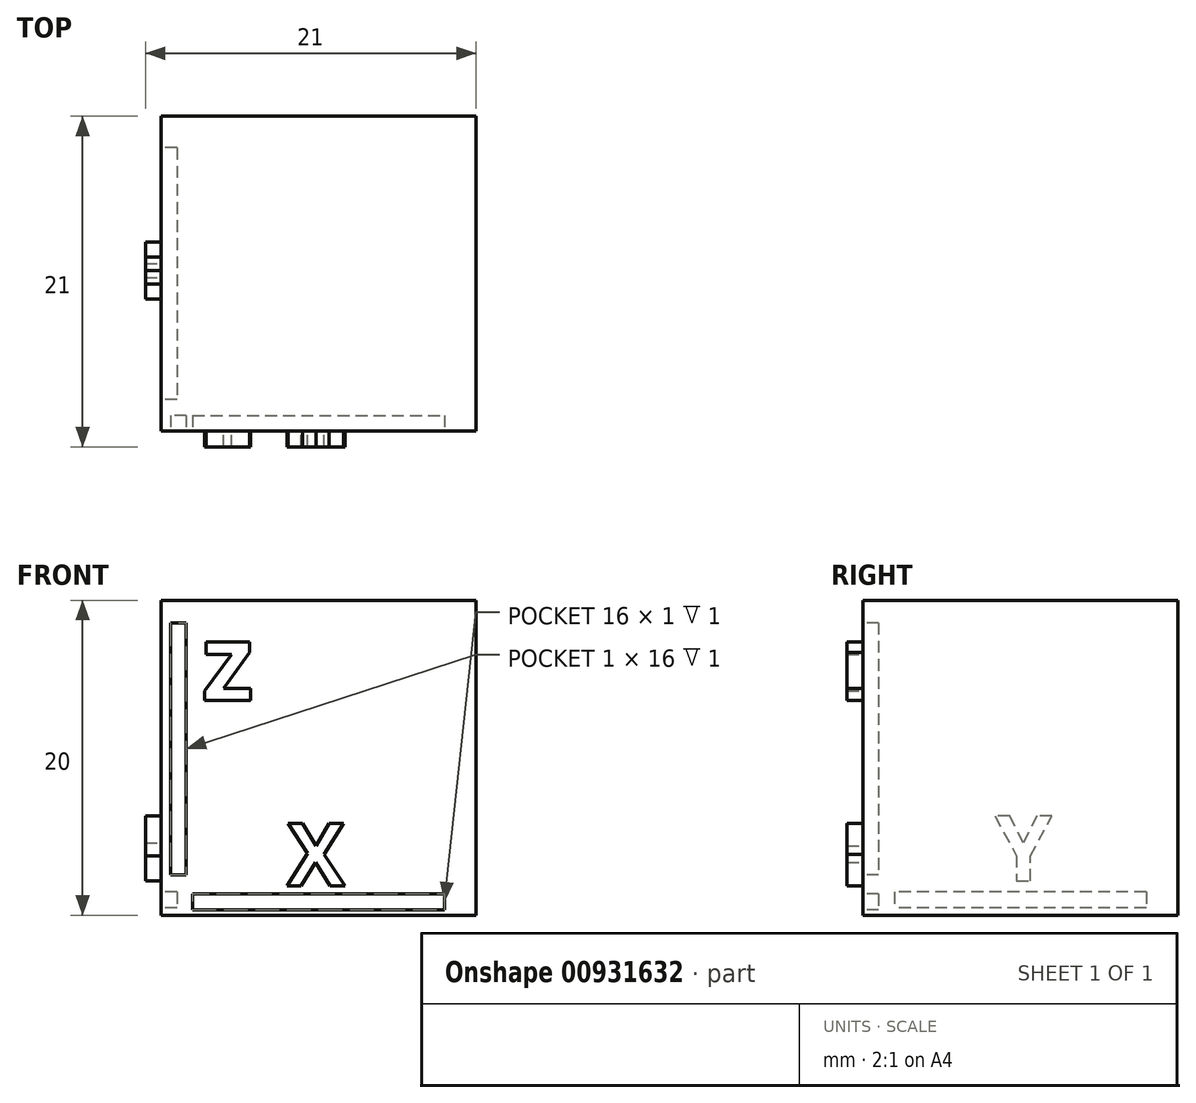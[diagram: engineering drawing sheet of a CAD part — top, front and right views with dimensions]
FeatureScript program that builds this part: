
annotation { "Feature Type Name" : "Feature", "Feature Type Description" : "" }
export const myFeature = defineFeature(function(context is Context, id is Id, definition is map)
    precondition{}
    {
        {
            var Q0;
            Q0=qCreatedBy(makeId("Top.planeOp"),FACE);
            var sketch = newSketch(context, id + "F0", { "sketchPlane" : qUnion([Q0])});
            skLineSegment(sketch, "E0.bottom", {"start": v(10, 10) * mm, "end": v(-10, 10) * mm});
            skLineSegment(sketch, "E0.top", {"start": v(10, -10) * mm, "end": v(-10, -10) * mm});
            skLineSegment(sketch, "E0.left", {"start": v(10, 10) * mm, "end": v(10, -10) * mm});
            skLineSegment(sketch, "E0.right", {"start": v(-10, 10) * mm, "end": v(-10, -10) * mm});
            skPoint(sketch, "E0.middle", {"position": v(0, 0) * mm});
            skSolve(sketch);
        }
        {
            var Q0;
            Q0=makeQuery(id+"F0.imprint","IMPRINT",FACE,{"disambiguationData":[TD([[makeQuery(id+"F0.imprint","IMPRINT",EDGE,{"derivedFrom":sQuery(id+"F0.wireOp",EDGE,"E0.bottom")}),1.0]])]});
            extrude(context, id + "F1", {"entities" : qUnion([Q0]), "depth" : 20 * mm, "offsetDistance" : 25 * mm});
        }
        {
            var Q0;
            Q0=makeQuery(id+"F1.opExtrude","SWEPT_FACE",FACE,{"disambiguationData":[OSD([sQuery(id+"F0.wireOp",EDGE,"E0.top")])]});
            var sketch = newSketch(context, id + "F2", { "sketchPlane" : qUnion([Q0])});
            skText(sketch, "E1", { "text": "z", "fontName": "OpenSans-Bold.ttf"});
            skText(sketch, "E2", { "text": "X", "fontName": "OpenSans-Bold.ttf"});
            skLineSegment(sketch, "E3.bottom", {"start": v(-8.4, 18.58) * mm, "end": v(-9.4, 18.58) * mm});
            skLineSegment(sketch, "E3.top", {"start": v(-8.4, 2.58) * mm, "end": v(-9.4, 2.58) * mm});
            skLineSegment(sketch, "E3.left", {"start": v(-8.4, 18.58) * mm, "end": v(-8.4, 2.58) * mm});
            skLineSegment(sketch, "E3.right", {"start": v(-9.4, 18.58) * mm, "end": v(-9.4, 2.58) * mm});
            skLineSegment(sketch, "E4.bottom", {"start": v(-8, 1.35) * mm, "end": v(8, 1.35) * mm});
            skLineSegment(sketch, "E4.top", {"start": v(-8, 0.35) * mm, "end": v(8, 0.35) * mm});
            skLineSegment(sketch, "E4.left", {"start": v(-8, 1.35) * mm, "end": v(-8, 0.35) * mm});
            skLineSegment(sketch, "E4.right", {"start": v(8, 1.35) * mm, "end": v(8, 0.35) * mm});
            skLineSegment(sketch, "E5", {"start": v(0, 0) * mm, "end": v(0, 20) * mm, "construction": true});
            const initialGuessF2  = {"E1": [-0.00743, 0.01364, 1, 0, 0.0049], "E2": [-0.00202, 0.00188, 1, 0, 0.00398]};
            skSetInitialGuess(sketch, initialGuessF2);
            skSolve(sketch);
        }
        {
            var Q0;
            Q0=makeQuery(id+"F1.opExtrude","SWEPT_FACE",FACE,{"disambiguationData":[OSD([sQuery(id+"F0.wireOp",EDGE,"E0.right")])]});
            var sketch = newSketch(context, id + "F3", { "sketchPlane" : qUnion([Q0])});
            skText(sketch, "E6", { "text": "Y", "fontName": "OpenSans-Bold.ttf"});
            skLineSegment(sketch, "E7.bottom", {"start": v(-8, 1.48) * mm, "end": v(8, 1.48) * mm});
            skLineSegment(sketch, "E7.top", {"start": v(-8, 0.48) * mm, "end": v(8, 0.48) * mm});
            skLineSegment(sketch, "E7.left", {"start": v(-8, 1.48) * mm, "end": v(-8, 0.48) * mm});
            skLineSegment(sketch, "E7.right", {"start": v(8, 1.48) * mm, "end": v(8, 0.48) * mm});
            skLineSegment(sketch, "E8", {"start": v(0, 0) * mm, "end": v(0, 20) * mm, "construction": true});
            skLineSegment(sketch, "E9", {"start": v(0, 1.48) * mm, "end": v(0, 0.48) * mm, "construction": true});
            const initialGuessF3  = {"E6": [-0.002, 0.00218, 1, 0, 0.00416]};
            skSetInitialGuess(sketch, initialGuessF3);
            skSolve(sketch);
        }
        {
            var Q0;
            Q0=makeQuery(id+"F2.imprint","IMPRINT",FACE,{"disambiguationData":[TD([[makeQuery(id+"F2.imprint","IMPRINT",EDGE,{"derivedFrom":sQuery(id+"F2.wireOp",EDGE,"E3.bottom")}),1.0]])]});
            var Q1;
            Q1=makeQuery(id+"F2.imprint","IMPRINT",FACE,{"disambiguationData":[TD([[makeQuery(id+"F2.imprint","IMPRINT",EDGE,{"derivedFrom":sQuery(id+"F2.wireOp",EDGE,"E4.bottom")}),-1.0]])]});
            extrude(context, id + "F4", {"entities" : qUnion([Q0, Q1]), "operationType" : NewBodyOperationType.REMOVE, "oppositeDirection" : true, "depth" : 1 * mm, "offsetDistance" : 25 * mm});
        }
        {
            var Q0;
            Q0=makeQuery(id+"F3.imprint","IMPRINT",FACE,{"disambiguationData":[TD([[makeQuery(id+"F3.imprint","IMPRINT",EDGE,{"derivedFrom":sQuery(id+"F3.wireOp",EDGE,"E7.bottom")}),-1.0]])]});
            extrude(context, id + "F5", {"entities" : qUnion([Q0]), "operationType" : NewBodyOperationType.REMOVE, "oppositeDirection" : true, "depth" : 1 * mm, "offsetDistance" : 25 * mm});
        }
        {
            var Q0;
            Q0=makeQuery(id+"F3.imprint","IMPRINT",FACE,{"disambiguationData":[TD([[makeQuery(id+"F3.imprint","IMPRINT",EDGE,{"derivedFrom":sQuery(id+"F3.wireOp",EDGE,"E6.sketch_text.stroke-0")}),-1.0]])]});
            extrude(context, id + "F6", {"entities" : qUnion([Q0]), "operationType" : NewBodyOperationType.ADD, "depth" : 1 * mm, "offsetDistance" : 25 * mm});
        }
        {
            var Q0;
            Q0=makeQuery(id+"F2.imprint","IMPRINT",FACE,{"disambiguationData":[TD([[makeQuery(id+"F2.imprint","IMPRINT",EDGE,{"derivedFrom":sQuery(id+"F2.wireOp",EDGE,"E1.sketch_text.stroke-0")}),-1.0]])]});
            var Q1;
            Q1=makeQuery(id+"F2.imprint","IMPRINT",FACE,{"disambiguationData":[TD([[makeQuery(id+"F2.imprint","IMPRINT",EDGE,{"derivedFrom":sQuery(id+"F2.wireOp",EDGE,"E2.sketch_text.stroke-0")}),-1.0]])]});
            extrude(context, id + "F7", {"entities" : qUnion([Q0, Q1]), "operationType" : NewBodyOperationType.ADD, "depth" : 1 * mm, "offsetDistance" : 25 * mm});
        }
    });
